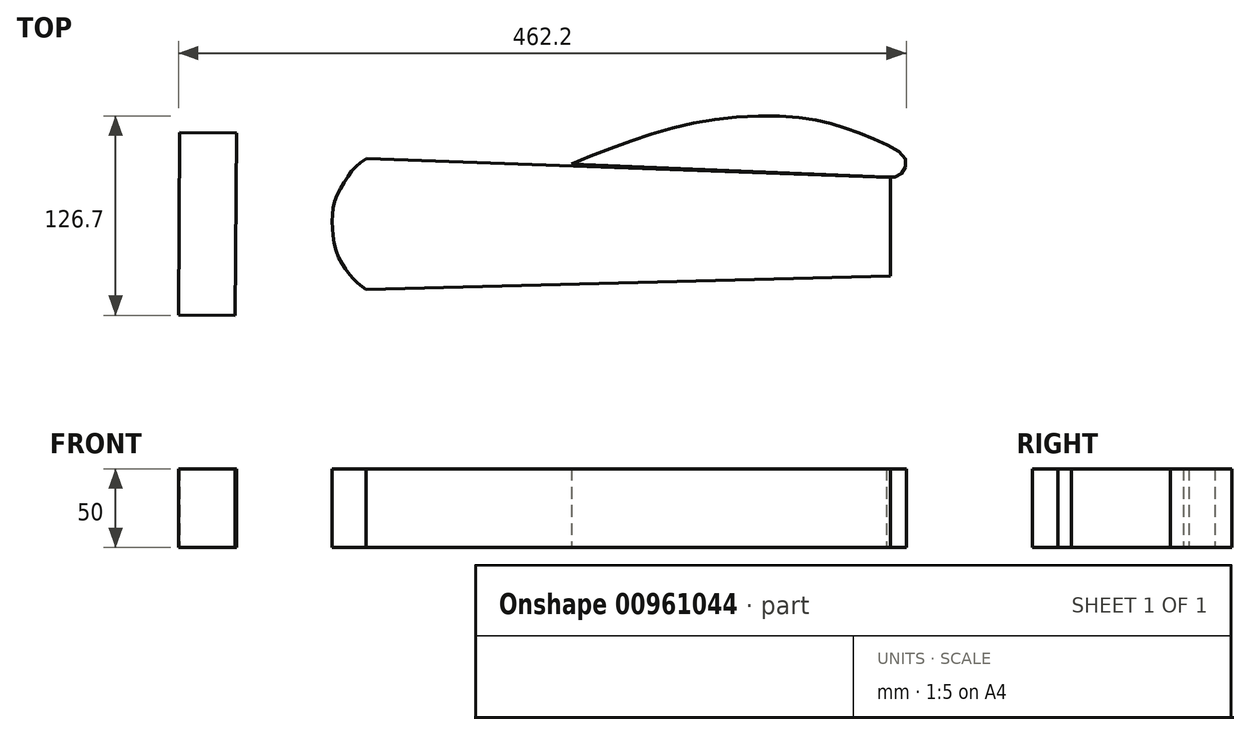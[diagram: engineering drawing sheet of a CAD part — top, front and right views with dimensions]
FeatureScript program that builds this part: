
annotation { "Feature Type Name" : "Feature", "Feature Type Description" : "" }
export const myFeature = defineFeature(function(context is Context, id is Id, definition is map)
    precondition{}
    {
        {
            var Q0;
            Q0=qCreatedBy(makeId("Top.planeOp"),FACE);
            var sketch = newSketch(context, id + "F0", { "sketchPlane" : qUnion([Q0])});
            skPoint(sketch, "E0.middle", {"position": v(0, 0) * mm});
            skFitSpline(sketch, "E1", {"points": [v(-239.8, 82.4) * mm, v(-213.31, 105.4) * mm, v(-178.46, 126.32) * mm, v(-145, 136.08) * mm, v(-101.77, 133.98) * mm, v(-64.82, 124.92) * mm, v(-23.73, 100.87) * mm, v(13.6, 74.2) * mm, v(39.69, 59.91) * mm, v(73.05, 66.53) * mm, v(100.34, 77.58) * mm, v(135.5, 87.67) * mm, v(174.1, 93.35) * mm, v(218.78, 93.71) * mm, v(272.13, 87.85) * mm, v(314.84, 71.62) * mm, v(336.04, 71.24) * mm, v(360.44, 56.6) * mm, v(361.83, 51.02) * mm, v(355.56, 41.96) * mm, v(340.92, 21.74) * mm, v(333.25, 0) * mm, v(332.55, -31.94) * mm, v(332.55, -32.63) * mm, v(323.5, -37.51) * mm, v(308.15, -35.42) * mm, v(303.27, -33.33) * mm], "startDerivative": vector(618.69, 612.62) * mm, "endDerivative": vector(245.75, -245.75) * mm});
            skLineSegment(sketch, "E2", {"start": v(301.88, -31.94) * mm, "end": v(7.68, -39.6) * mm});
            skFitSpline(sketch, "E3", {"points": [v(7.68, -39.6) * mm, v(-9.75, -43.79) * mm, v(-24.39, -52.15) * mm, v(-30.66, -57.73) * mm, v(-29.96, -64.7) * mm, v(-19.5, -73.77) * mm, v(-0.68, -87.01) * mm, v(8.38, -102.35) * mm, v(7.68, -111.41) * mm, v(0, -110.27) * mm, v(0, -110.27) * mm, v(-19.43, -97.27) * mm, v(-29.3, -93.11) * mm, v(-39.18, -90) * mm, v(-53.67, -88.4) * mm, v(-81.29, -93.63) * mm, v(-90.12, -97.27) * mm, v(-100, -102.47) * mm, v(-126, -118.59) * mm, v(-151.99, -135.22) * mm, v(-186.3, -118.59) * mm, v(-228.4, -95.2) * mm, v(-258.63, -78.65) * mm, v(-257.23, -66.1) * mm, v(-248.87, -60.52) * mm, v(-239.1, -52.15) * mm, v(-234.92, -46.58) * mm, v(-234.92, 55.9) * mm, v(-235.62, 62.87) * mm, v(-239.8, 69.15) * mm, v(-239.8, 82.4) * mm], "startDerivative": vector(-530.9, -85.09) * mm, "endDerivative": vector(291.54, 801.75) * mm});
            skFitSpline(sketch, "E4", {"points": [v(110.16, 40.57) * mm, v(158.27, 58.7) * mm, v(209.16, 69.85) * mm, v(257.26, 69.85) * mm, v(283.75, 63.57) * mm, v(308.15, 53.81) * mm, v(322.1, 44.75) * mm, v(322.1, 37.78) * mm, v(317.91, 32.9) * mm, v(310.24, 32.2) * mm], "startDerivative": vector(268.52, 112.98) * mm, "endDerivative": vector(-130.09, 6.83) * mm});
            skLineSegment(sketch, "E5", {"start": v(310.24, 32.2) * mm, "end": v(110.16, 40.57) * mm});
            skLineSegment(sketch, "E6", {"start": v(303.27, -33.33) * mm, "end": v(301.88, -31.94) * mm});
            skFitSpline(sketch, "E7", {"points": [v(-19.75, 43.96) * mm, v(-28.07, 37.72) * mm, v(-34.3, 28.36) * mm, v(-40.03, 17.44) * mm, v(-41.59, 6.53) * mm, v(-41.07, -5.43) * mm, v(-37.43, -18.94) * mm, v(-31.7, -28.3) * mm, v(-25.47, -35.06) * mm, v(-20.27, -39.22) * mm], "startDerivative": vector(-94.86, -60.12) * mm, "endDerivative": vector(59.6, -44.4) * mm});
            skLineSegment(sketch, "E8", {"start": v(-19.75, 43.96) * mm, "end": v(313, 32.06) * mm});
            skLineSegment(sketch, "E9", {"start": v(313, -30.58) * mm, "end": v(-20.27, -39.22) * mm});
            skLineSegment(sketch, "E10", {"start": v(313, 32.06) * mm, "end": v(313, -30.58) * mm});
            skLineSegment(sketch, "E11", {"start": v(-138.55, 60.62) * mm, "end": v(-139.29, -55.31) * mm});
            skLineSegment(sketch, "E12", {"start": v(-139.29, -55.31) * mm, "end": v(-103.24, -55.55) * mm});
            skLineSegment(sketch, "E13", {"start": v(-103.24, -55.55) * mm, "end": v(-102.5, 60.4) * mm});
            skLineSegment(sketch, "E14", {"start": v(-102.5, 60.4) * mm, "end": v(-138.55, 60.62) * mm});
            skSolve(sketch);
        }
        {
            var Q0;
            Q0=qSketchRegion(id+"F0",true);
            extrude(context, id + "F1", {"entities" : qUnion([Q0]), "depth" : 50 * mm, "offsetDistance" : 25 * mm});
        }
    });
